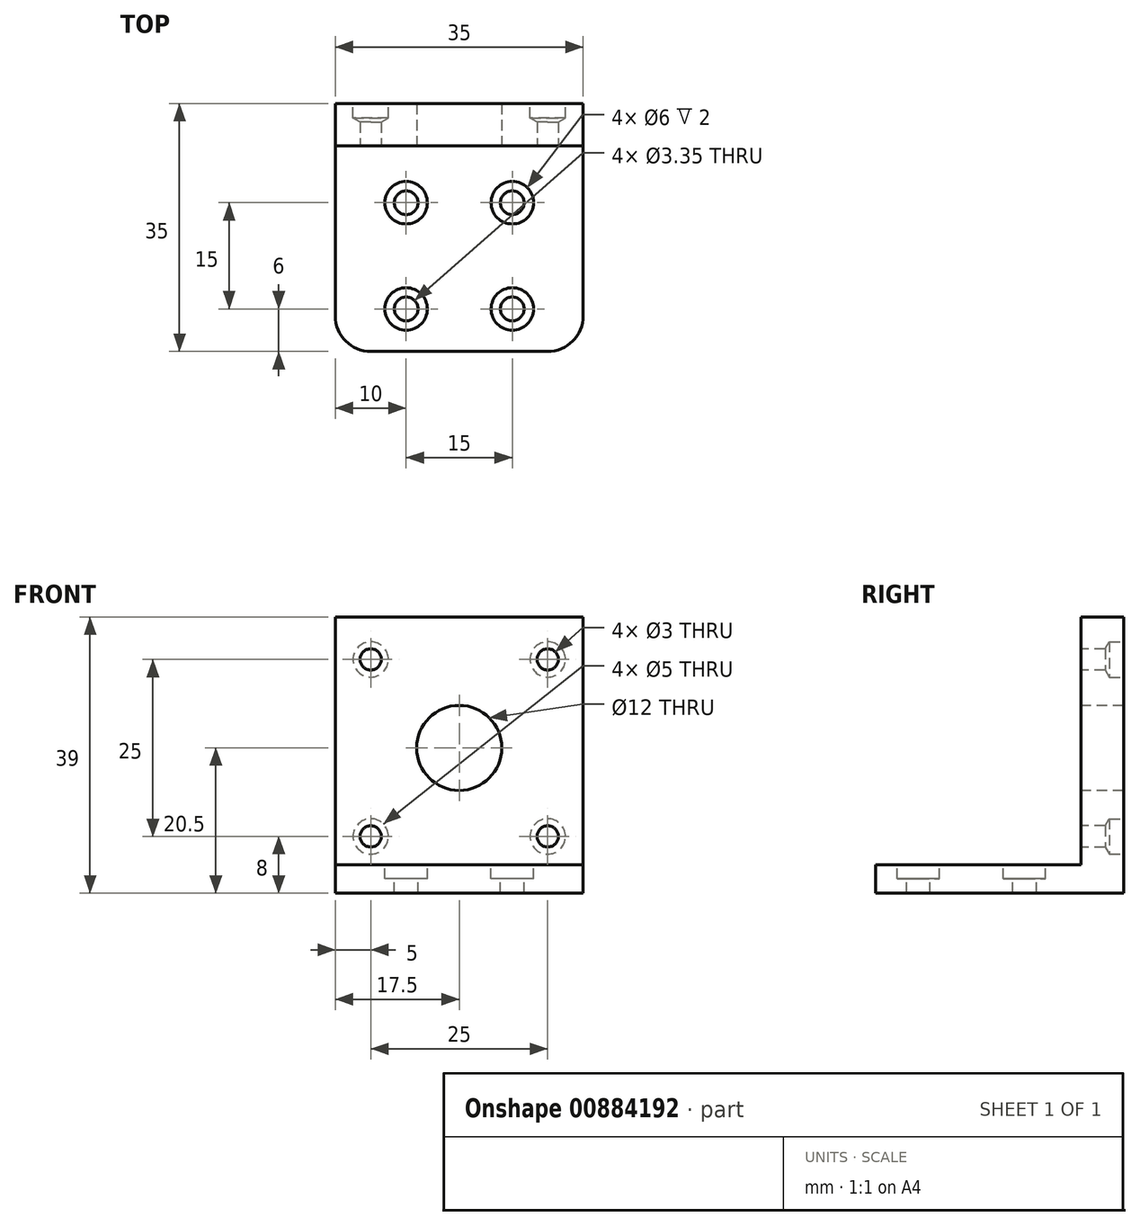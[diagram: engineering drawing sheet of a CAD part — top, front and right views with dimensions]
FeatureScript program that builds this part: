
annotation { "Feature Type Name" : "Feature", "Feature Type Description" : "" }
export const myFeature = defineFeature(function(context is Context, id is Id, definition is map)
    precondition{}
    {
        {
            var Q0;
            Q0=qCreatedBy(makeId("Top.planeOp"),FACE);
            var sketch = newSketch(context, id + "F0", { "sketchPlane" : qUnion([Q0])});
            skLineSegment(sketch, "E0.bottom", {"start": v(0, 0) * mm, "end": v(35, 0) * mm});
            skLineSegment(sketch, "E0.top", {"start": v(0, 35) * mm, "end": v(35, 35) * mm});
            skLineSegment(sketch, "E0.left", {"start": v(0, 0) * mm, "end": v(0, 35) * mm});
            skLineSegment(sketch, "E0.right", {"start": v(35, 0) * mm, "end": v(35, 35) * mm});
            skSolve(sketch);
        }
        {
            var Q0;
            Q0=qSketchRegion(id+"F0",true);
            extrude(context, id + "F1", {"entities" : qUnion([Q0]), "depth" : 4 * mm});
        }
        {
            var Q0;
            Q0=makeQuery(id+"F1.opExtrude","CAP_FACE",FACE,{"disambiguationData":[OSD([sQuery(id+"F0.wireOp",EDGE,"E0.bottom"),sQuery(id+"F0.wireOp",EDGE,"E0.top"),sQuery(id+"F0.wireOp",EDGE,"E0.left"),sQuery(id+"F0.wireOp",EDGE,"E0.right")])],"isStart":false});
            var sketch = newSketch(context, id + "F2", { "sketchPlane" : qUnion([Q0])});
            skCircle(sketch, "E1", {"center": v(10, 21) * mm, "radius": 1.68 * mm});
            skCircle(sketch, "E2", {"center": v(25, 21) * mm, "radius": 1.68 * mm});
            skCircle(sketch, "E3", {"center": v(10, 6) * mm, "radius": 1.68 * mm});
            skCircle(sketch, "E4", {"center": v(25, 6) * mm, "radius": 1.68 * mm});
            skLineSegment(sketch, "E5", {"start": v(10, 21) * mm, "end": v(0, 21) * mm});
            skLineSegment(sketch, "E6", {"start": v(25, 6) * mm, "end": v(35, 6) * mm});
            skCircle(sketch, "E7", {"center": v(10, 21) * mm, "radius": 3 * mm});
            skCircle(sketch, "E8", {"center": v(25, 21) * mm, "radius": 3 * mm});
            skCircle(sketch, "E9", {"center": v(10, 6) * mm, "radius": 3 * mm});
            skCircle(sketch, "E10", {"center": v(25, 6) * mm, "radius": 3 * mm});
            skLineSegment(sketch, "E11", {"start": v(10, 6) * mm, "end": v(10, 0) * mm});
            skSolve(sketch);
        }
        {
            var Q0;
            Q0=makeQuery(id+"F1.opExtrude","CAP_FACE",FACE,{"disambiguationData":[OSD([sQuery(id+"F0.wireOp",EDGE,"E0.bottom"),sQuery(id+"F0.wireOp",EDGE,"E0.top"),sQuery(id+"F0.wireOp",EDGE,"E0.left"),sQuery(id+"F0.wireOp",EDGE,"E0.right")])],"isStart":false});
            var sketch = newSketch(context, id + "F3", { "sketchPlane" : qUnion([Q0])});
            skLineSegment(sketch, "E12.bottom", {"start": v(0, 35) * mm, "end": v(35, 35) * mm});
            skLineSegment(sketch, "E12.top", {"start": v(0, 29) * mm, "end": v(35, 29) * mm});
            skLineSegment(sketch, "E12.left", {"start": v(0, 35) * mm, "end": v(0, 29) * mm});
            skLineSegment(sketch, "E12.right", {"start": v(35, 35) * mm, "end": v(35, 29) * mm});
            skSolve(sketch);
        }
        {
            var Q0;
            Q0=makeQuery(id+"F2.imprint","IMPRINT",FACE,{"disambiguationData":[TD([[makeQuery(id+"F2.imprint","IMPRINT",EDGE,{"derivedFrom":sQuery(id+"F2.wireOp",EDGE,"E1")}),-1.0]])]});
            var Q1;
            Q1=makeQuery(id+"F2.imprint","IMPRINT",FACE,{"disambiguationData":[TD([[makeQuery(id+"F2.imprint","IMPRINT",EDGE,{"derivedFrom":sQuery(id+"F2.wireOp",EDGE,"E2")}),-1.0]])]});
            var Q2;
            Q2=makeQuery(id+"F2.imprint","IMPRINT",FACE,{"disambiguationData":[TD([[makeQuery(id+"F2.imprint","IMPRINT",EDGE,{"derivedFrom":sQuery(id+"F2.wireOp",EDGE,"E4")}),-1.0]])]});
            var Q3;
            Q3=makeQuery(id+"F2.imprint","IMPRINT",FACE,{"disambiguationData":[TD([[makeQuery(id+"F2.imprint","IMPRINT",EDGE,{"derivedFrom":sQuery(id+"F2.wireOp",EDGE,"E3")}),-1.0]])]});
            extrude(context, id + "F4", {"entities" : qUnion([Q0, Q1, Q2, Q3]), "operationType" : NewBodyOperationType.REMOVE, "oppositeDirection" : true, "depth" : 2 * mm});
        }
        {
            var Q0;
            Q0=makeQuery(id+"F1.opExtrude","SWEPT_EDGE",EDGE,{"disambiguationData":[OSD([sQuery(id+"F0.wireOp",EDGE,"E0.bottom"),sQuery(id+"F0.wireOp",EDGE,"E0.left")])]});
            var Q1;
            Q1=makeQuery(id+"F1.opExtrude","SWEPT_EDGE",EDGE,{"disambiguationData":[OSD([sQuery(id+"F0.wireOp",EDGE,"E0.bottom"),sQuery(id+"F0.wireOp",EDGE,"E0.right")])]});
            fillet(context, id + "F5", {"entities" : qUnion([Q0, Q1]), "radius" : 5 * mm, "tangentPropagation" : true, "allowEdgeOverflow" : false});
        }
        {
            var Q0;
            Q0=makeQuery(id+"F2.imprint","IMPRINT",FACE,{"disambiguationData":[TD([[makeQuery(id+"F2.imprint","IMPRINT",EDGE,{"derivedFrom":sQuery(id+"F2.wireOp",EDGE,"E1")}),1.0]])]});
            var Q1;
            Q1=makeQuery(id+"F2.imprint","IMPRINT",FACE,{"disambiguationData":[TD([[makeQuery(id+"F2.imprint","IMPRINT",EDGE,{"derivedFrom":sQuery(id+"F2.wireOp",EDGE,"E2")}),1.0]])]});
            var Q2;
            Q2=makeQuery(id+"F2.imprint","IMPRINT",FACE,{"disambiguationData":[TD([[makeQuery(id+"F2.imprint","IMPRINT",EDGE,{"derivedFrom":sQuery(id+"F2.wireOp",EDGE,"E4")}),1.0]])]});
            var Q3;
            Q3=makeQuery(id+"F2.imprint","IMPRINT",FACE,{"disambiguationData":[TD([[makeQuery(id+"F2.imprint","IMPRINT",EDGE,{"derivedFrom":sQuery(id+"F2.wireOp",EDGE,"E3")}),1.0]])]});
            extrude(context, id + "F6", {"entities" : qUnion([Q0, Q1, Q2, Q3]), "operationType" : NewBodyOperationType.REMOVE, "oppositeDirection" : true, "depth" : 25 * mm, "symmetric" : true});
        }
        {
            var Q0;
            Q0=makeQuery(id+"F3.imprint","IMPRINT",FACE,{"disambiguationData":[TD([[makeQuery(id+"F3.imprint","IMPRINT",EDGE,{"derivedFrom":sQuery(id+"F3.wireOp",EDGE,"E12.bottom")}),-1.0]])]});
            extrude(context, id + "F7", {"entities" : qUnion([Q0]), "operationType" : NewBodyOperationType.ADD, "depth" : 35 * mm});
        }
        {
            var Q0;
            Q0=makeQuery(id+"F7.opExtrude","SWEPT_FACE",FACE,{"disambiguationData":[OSD([sQuery(id+"F3.wireOp",EDGE,"E12.top")])]});
            var sketch = newSketch(context, id + "F8", { "sketchPlane" : qUnion([Q0])});
            skLineSegment(sketch, "E13", {"start": v(17.5, 4) * mm, "end": v(1, 4) * mm, "construction": true});
            skLineSegment(sketch, "E14", {"start": v(1, 4) * mm, "end": v(1, 37) * mm, "construction": true});
            skLineSegment(sketch, "E15", {"start": v(1, 37) * mm, "end": v(34, 37) * mm, "construction": true});
            skLineSegment(sketch, "E16", {"start": v(34, 37) * mm, "end": v(34, 4) * mm, "construction": true});
            skLineSegment(sketch, "E17", {"start": v(1, 37) * mm, "end": v(34, 4) * mm, "construction": true});
            skLineSegment(sketch, "E18", {"start": v(34, 37) * mm, "end": v(1, 4) * mm, "construction": true});
            skCircle(sketch, "E19", {"center": v(17.5, 20.5) * mm, "radius": 6 * mm});
            skLineSegment(sketch, "E20", {"start": v(17.5, 4) * mm, "end": v(17.5, 8) * mm, "construction": true});
            skLineSegment(sketch, "E21", {"start": v(17.5, 8) * mm, "end": v(5, 8) * mm});
            skLineSegment(sketch, "E22", {"start": v(5, 8) * mm, "end": v(30, 8) * mm, "construction": true});
            skLineSegment(sketch, "E23", {"start": v(30, 8) * mm, "end": v(30, 33) * mm, "construction": true});
            skLineSegment(sketch, "E24", {"start": v(30, 33) * mm, "end": v(5, 33) * mm, "construction": true});
            skCircle(sketch, "E25", {"center": v(5, 33) * mm, "radius": 1.5 * mm});
            skCircle(sketch, "E26", {"center": v(30, 33) * mm, "radius": 1.5 * mm});
            skCircle(sketch, "E27", {"center": v(30, 8) * mm, "radius": 1.5 * mm});
            skCircle(sketch, "E28", {"center": v(5, 8) * mm, "radius": 1.5 * mm});
            skSolve(sketch);
        }
        {
            var Q0;
            Q0=makeQuery(id+"F8.imprint","IMPRINT",FACE,{"disambiguationData":[TD([[makeQuery(id+"F8.imprint","IMPRINT",EDGE,{"derivedFrom":sQuery(id+"F8.wireOp",EDGE,"E19")}),1.0]])]});
            var Q1;
            Q1=makeQuery(id+"F8.imprint","IMPRINT",FACE,{"disambiguationData":[TD([[makeQuery(id+"F8.imprint","IMPRINT",EDGE,{"derivedFrom":sQuery(id+"F8.wireOp",EDGE,"E26")}),1.0]])]});
            var Q2;
            Q2=makeQuery(id+"F8.imprint","IMPRINT",FACE,{"disambiguationData":[TD([[makeQuery(id+"F8.imprint","IMPRINT",EDGE,{"derivedFrom":sQuery(id+"F8.wireOp",EDGE,"E25")}),1.0]])]});
            var Q3;
            Q3=makeQuery(id+"F8.imprint","IMPRINT",FACE,{"disambiguationData":[TD([[makeQuery(id+"F8.imprint","IMPRINT",EDGE,{"derivedFrom":sQuery(id+"F8.wireOp",EDGE,"E28")}),1.0]])]});
            var Q4;
            Q4=makeQuery(id+"F8.imprint","IMPRINT",FACE,{"disambiguationData":[TD([[makeQuery(id+"F8.imprint","IMPRINT",EDGE,{"derivedFrom":sQuery(id+"F8.wireOp",EDGE,"E27")}),1.0]])]});
            var Q5;
            Q5=sQuery(id+"F8.wireOp",EDGE,"E19");
            extrude(context, id + "F9", {"entities" : qUnion([Q0, Q1, Q2, Q3, Q4]), "operationType" : NewBodyOperationType.REMOVE, "surfaceEntities" : qUnion([Q5]), "endBound" : BoundingType.THROUGH_ALL, "oppositeDirection" : true, "depth" : 25 * mm});
        }
        {
            var Q0;
            Q0=makeQuery(id+"F7.boolean.opBoolean","MERGE",FACE,{"derivedFrom":[makeQuery(id+"F1.opExtrude","SWEPT_FACE",FACE,{"disambiguationData":[OSD([sQuery(id+"F0.wireOp",EDGE,"E0.top")])]}),makeQuery(id+"F7.opExtrude","SWEPT_FACE",FACE,{"disambiguationData":[OSD([sQuery(id+"F3.wireOp",EDGE,"E12.bottom")])]})]});
            var sketch = newSketch(context, id + "F10", { "sketchPlane" : qUnion([Q0])});
            skLineSegment(sketch, "E29", {"start": v(-30, 33) * mm, "end": v(-5, 33) * mm, "construction": true});
            skLineSegment(sketch, "E30", {"start": v(-5, 33) * mm, "end": v(-5, 8) * mm, "construction": true});
            skLineSegment(sketch, "E31", {"start": v(-5, 8) * mm, "end": v(-30, 8) * mm, "construction": true});
            skLineSegment(sketch, "E32", {"start": v(-30, 8) * mm, "end": v(-30, 33) * mm, "construction": true});
            skSolve(sketch);
        }
        {
            var Q0;
            Q0=sQuery(id+"F10.wireOp",VERTEX,"E32.end");
            var Q1;
            Q1=sQuery(id+"F10.wireOp",VERTEX,"E32.start");
            var Q2;
            Q2=sQuery(id+"F10.wireOp",VERTEX,"E31.start");
            var Q3;
            Q3=sQuery(id+"F10.wireOp",VERTEX,"E30.start");
            var Q4;
            Q4=makeQuery(id+"F1.opExtrude","SWEPT_BODY",BODY,{"disambiguationData":[OSD([sQuery(id+"F0.wireOp",EDGE,"E0.bottom"),sQuery(id+"F0.wireOp",EDGE,"E0.top"),sQuery(id+"F0.wireOp",EDGE,"E0.left"),sQuery(id+"F0.wireOp",EDGE,"E0.right")])]});
            hole(context, id + "F11", {"style" : HoleStyle.SIMPLE, "endStyle" : HoleEndStyle.BLIND, "holeDiameter" : 5 * mm, "holeDepth" : 2 * mm, "isTappedThrough" : true, "tappedDepth" : 12 * mm, "tapClearance" : 3, "locations" : qUnion([Q0, Q1, Q2, Q3]), "scope" : qUnion([Q4])});
        }
    });
